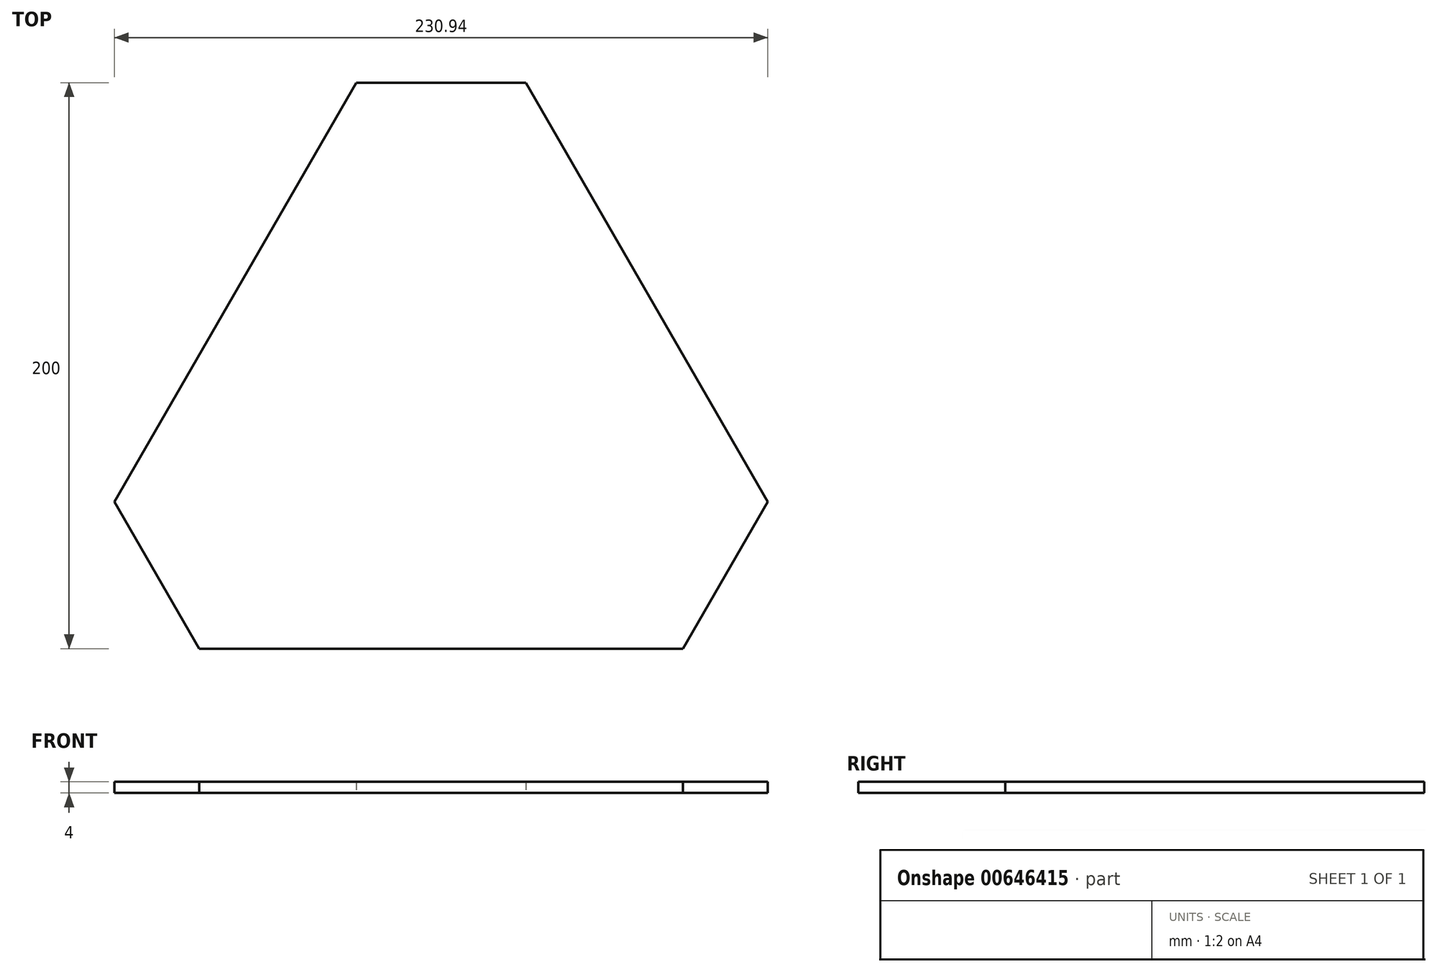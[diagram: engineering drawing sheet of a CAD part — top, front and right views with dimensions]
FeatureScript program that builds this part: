
annotation { "Feature Type Name" : "Feature", "Feature Type Description" : "" }
export const myFeature = defineFeature(function(context is Context, id is Id, definition is map)
    precondition{}
    {
        {
            var Q0;
            Q0=qCreatedBy(makeId("Top.planeOp"),FACE);
            var sketch = newSketch(context, id + "F0", { "sketchPlane" : qUnion([Q0])});
            skLineSegment(sketch, "E0.0", {"start": v(30, 81.37) * mm, "end": v(115.47, -66.67) * mm});
            skLineSegment(sketch, "E0.1", {"start": v(85.47, -118.63) * mm, "end": v(-85.47, -118.63) * mm});
            skLineSegment(sketch, "E0.2", {"start": v(-115.47, -66.67) * mm, "end": v(-30, 81.37) * mm});
            skLineSegment(sketch, "E1", {"start": v(-30, 81.37) * mm, "end": v(30, 81.37) * mm});
            skLineSegment(sketch, "E2.1.0", {"start": v(-85.47, -118.63) * mm, "end": v(-115.47, -66.67) * mm});
            skLineSegment(sketch, "E2.2.0", {"start": v(115.47, -66.67) * mm, "end": v(85.47, -118.63) * mm});
            skPoint(sketch, "E2.center", {"position": v(0, -34.64) * mm});
            skPoint(sketch, "E3.orphan", {"position": v(0, 133.33) * mm});
            skPoint(sketch, "E4.orphan", {"position": v(-145.47, -118.63) * mm});
            skPoint(sketch, "E5.orphan", {"position": v(145.47, -118.63) * mm});
            skSolve(sketch);
        }
        {
            var Q0;
            Q0=makeQuery(id+"F0.imprint","IMPRINT",FACE,{"disambiguationData":[TD([[makeQuery(id+"F0.imprint","IMPRINT",EDGE,{"derivedFrom":sQuery(id+"F0.wireOp",EDGE,"E0.0")}),-1.0]])]});
            extrude(context, id + "F1", {"entities" : qUnion([Q0]), "depth" : 4 * mm, "offsetDistance" : 25 * mm});
        }
    });
